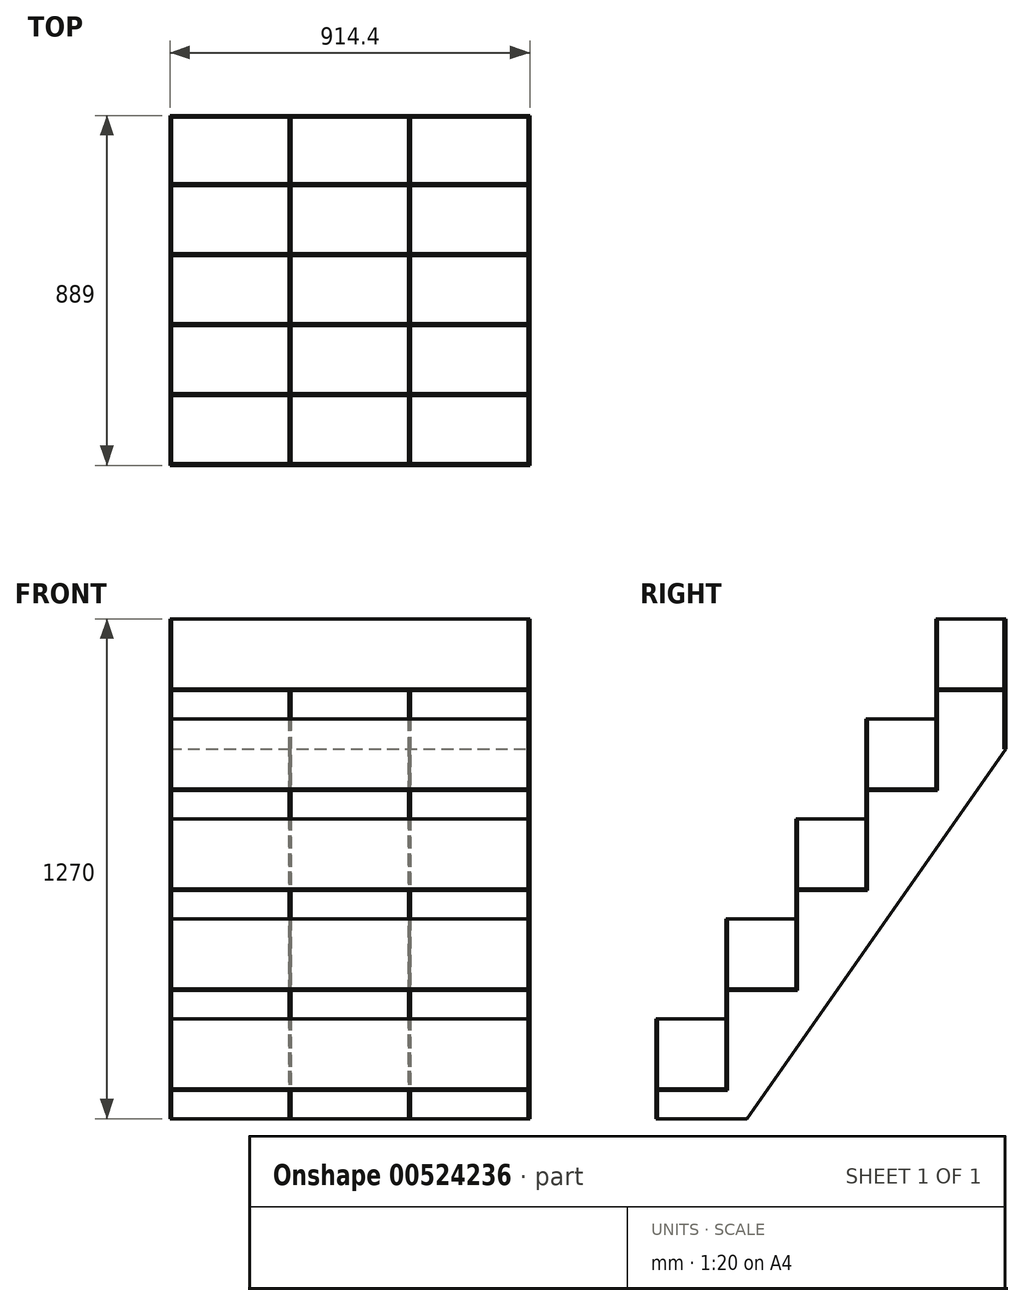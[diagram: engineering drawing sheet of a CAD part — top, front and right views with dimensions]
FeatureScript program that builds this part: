
annotation { "Feature Type Name" : "Feature", "Feature Type Description" : "" }
export const myFeature = defineFeature(function(context is Context, id is Id, definition is map)
    precondition{}
    {
        {
            assignVariable(context, id + "F0", {"name" : "matthick", "anyValue" : 4.7 * mm});
        }
        {
            var Q0;
            Q0=qCreatedBy(makeId("Right.planeOp"),FACE);
            var sketch = newSketch(context, id + "F1", { "sketchPlane" : qUnion([Q0])});
            skLineSegment(sketch, "E0", {"start": v(-436.82, -657.41) * mm, "end": v(-205.43, -657.41) * mm});
            skLineSegment(sketch, "E1", {"start": v(-205.43, -657.41) * mm, "end": v(452.18, 281.76) * mm});
            skLineSegment(sketch, "E2", {"start": v(452.18, 281.76) * mm, "end": v(452.18, 612.59) * mm});
            skLineSegment(sketch, "E3", {"start": v(452.18, 612.59) * mm, "end": v(274.38, 612.59) * mm});
            skLineSegment(sketch, "E4", {"start": v(274.38, 612.59) * mm, "end": v(274.38, 358.59) * mm});
            skLineSegment(sketch, "E5", {"start": v(274.38, 358.59) * mm, "end": v(96.58, 358.59) * mm});
            skLineSegment(sketch, "E6", {"start": v(96.58, 358.59) * mm, "end": v(96.58, 104.59) * mm});
            skLineSegment(sketch, "E7", {"start": v(96.58, 104.59) * mm, "end": v(-81.22, 104.59) * mm});
            skLineSegment(sketch, "E8", {"start": v(-81.22, 104.59) * mm, "end": v(-81.22, -149.41) * mm});
            skLineSegment(sketch, "E9", {"start": v(-81.22, -149.41) * mm, "end": v(-259.02, -149.41) * mm});
            skLineSegment(sketch, "E10", {"start": v(-259.02, -149.41) * mm, "end": v(-259.02, -403.41) * mm});
            skLineSegment(sketch, "E11", {"start": v(-259.02, -403.41) * mm, "end": v(-436.82, -403.41) * mm});
            skLineSegment(sketch, "E12", {"start": v(-436.82, -403.41) * mm, "end": v(-436.82, -657.41) * mm});
            skSolve(sketch);
        }
        {
            var Q0;
            Q0=qSketchRegion(id+"F1",true);
            extrude(context, id + "F2", {"entities" : qUnion([Q0]), "depth" : getVariable(context, 'matthick'), "offsetDistance" : 25.4 * mm});
        }
        {
            var Q0;
            Q0=makeQuery(id+"F2.opExtrude","CAP_FACE",FACE,{"disambiguationData":[OSD([sQuery(id+"F1.wireOp",EDGE,"E0"),sQuery(id+"F1.wireOp",EDGE,"E1"),sQuery(id+"F1.wireOp",EDGE,"E2"),sQuery(id+"F1.wireOp",EDGE,"E3"),sQuery(id+"F1.wireOp",EDGE,"E4"),sQuery(id+"F1.wireOp",EDGE,"E5"),sQuery(id+"F1.wireOp",EDGE,"E6"),sQuery(id+"F1.wireOp",EDGE,"E7"),sQuery(id+"F1.wireOp",EDGE,"E8"),sQuery(id+"F1.wireOp",EDGE,"E9"),sQuery(id+"F1.wireOp",EDGE,"E10"),sQuery(id+"F1.wireOp",EDGE,"E11"),sQuery(id+"F1.wireOp",EDGE,"E12")])],"isStart":false});
            var sketch = newSketch(context, id + "F3", { "sketchPlane" : qUnion([Q0])});
            skLineSegment(sketch, "E13", {"start": v(274.38, 612.59) * mm, "end": v(274.38, 434.79) * mm, "construction": true});
            skLineSegment(sketch, "E14.bottom", {"start": v(274.38, 434.79) * mm, "end": v(452.18, 434.79) * mm});
            skLineSegment(sketch, "E14.top", {"start": v(274.38, 430.09) * mm, "end": v(452.18, 430.09) * mm});
            skLineSegment(sketch, "E14.left", {"start": v(274.38, 434.79) * mm, "end": v(274.38, 430.09) * mm});
            skLineSegment(sketch, "E14.right", {"start": v(452.18, 434.79) * mm, "end": v(452.18, 430.09) * mm});
            skSolve(sketch);
        }
        {
            var Q0;
            Q0=makeQuery(id+"F3.imprint","IMPRINT",FACE,{"disambiguationData":[TD([[makeQuery(id+"F3.imprint","IMPRINT",EDGE,{"derivedFrom":sQuery(id+"F3.wireOp",EDGE,"E14.bottom")}),-1.0]])]});
            extrude(context, id + "F4", {"entities" : qUnion([Q0]), "oppositeDirection" : true, "depth" : 914.4 * mm, "offsetDistance" : 25.4 * mm});
        }
        {
            var Q0;
            Q0=makeQuery(id+"F4.opExtrude","SWEPT_BODY",BODY,{"disambiguationData":[OSD([sQuery(id+"F3.wireOp",EDGE,"E14.bottom"),sQuery(id+"F3.wireOp",EDGE,"E14.top"),sQuery(id+"F3.wireOp",EDGE,"E14.left"),sQuery(id+"F3.wireOp",EDGE,"E14.right")])]});
            var Q1;
            Q1=sQuery(id+"F1.wireOp",EDGE,"E4");
            var Q2;
            Q2=sQuery(id+"F1.wireOp",EDGE,"E5");
            transform(context, id + "F5", {"entities" : qUnion([Q0]), "transformType" : TransformType.TRANSLATION_3D, "dx" : 0 * mm, "dy" : -177.8 * mm, "dz" : -254 * mm, "makeCopy" : true});
        }
        {
            var Q0;
            Q0=makeQuery(id+"F2.opExtrude","CAP_FACE",FACE,{"disambiguationData":[OSD([sQuery(id+"F1.wireOp",EDGE,"E0"),sQuery(id+"F1.wireOp",EDGE,"E1"),sQuery(id+"F1.wireOp",EDGE,"E2"),sQuery(id+"F1.wireOp",EDGE,"E3"),sQuery(id+"F1.wireOp",EDGE,"E4"),sQuery(id+"F1.wireOp",EDGE,"E5"),sQuery(id+"F1.wireOp",EDGE,"E6"),sQuery(id+"F1.wireOp",EDGE,"E7"),sQuery(id+"F1.wireOp",EDGE,"E8"),sQuery(id+"F1.wireOp",EDGE,"E9"),sQuery(id+"F1.wireOp",EDGE,"E10"),sQuery(id+"F1.wireOp",EDGE,"E11"),sQuery(id+"F1.wireOp",EDGE,"E12")])],"isStart":false});
            var sketch = newSketch(context, id + "F6", { "sketchPlane" : qUnion([Q0])});
            skLineSegment(sketch, "E15.bottom", {"start": v(274.38, 612.59) * mm, "end": v(279.08, 612.59) * mm});
            skLineSegment(sketch, "E15.top", {"start": v(274.38, 176.09) * mm, "end": v(279.08, 176.09) * mm});
            skLineSegment(sketch, "E15.left", {"start": v(274.38, 612.59) * mm, "end": v(274.38, 176.09) * mm});
            skLineSegment(sketch, "E15.right", {"start": v(279.08, 612.59) * mm, "end": v(279.08, 176.09) * mm});
            skSolve(sketch);
        }
        {
            var Q0;
            Q0=qSketchRegion(id+"F6",true);
            extrude(context, id + "F7", {"entities" : qUnion([Q0]), "oppositeDirection" : true, "depth" : 914.4 * mm, "offsetDistance" : 25.4 * mm});
        }
        {
            var Q0;
            Q0=makeQuery(id+"F5.opPattern","COPY",BODY,{"derivedFrom":makeQuery(id+"F4.opExtrude","SWEPT_BODY",BODY,{"disambiguationData":[OSD([sQuery(id+"F3.wireOp",EDGE,"E14.bottom"),sQuery(id+"F3.wireOp",EDGE,"E14.top"),sQuery(id+"F3.wireOp",EDGE,"E14.left"),sQuery(id+"F3.wireOp",EDGE,"E14.right")])]}),"instanceName":"1"});
            var Q1;
            Q1=makeQuery(id+"F7.opExtrude","SWEPT_BODY",BODY,{"disambiguationData":[OSD([sQuery(id+"F6.wireOp",EDGE,"E15.bottom"),sQuery(id+"F6.wireOp",EDGE,"E15.top"),sQuery(id+"F6.wireOp",EDGE,"E15.left"),sQuery(id+"F6.wireOp",EDGE,"E15.right")])]});
            transform(context, id + "F8", {"entities" : qUnion([Q0, Q1]), "transformType" : TransformType.TRANSLATION_3D, "dx" : 0 * mm, "dy" : -177.8 * mm, "dz" : -254 * mm, "makeCopy" : true});
        }
        {
            var Q0;
            Q0=makeQuery(id+"F8.opPattern","COPY",BODY,{"derivedFrom":makeQuery(id+"F5.opPattern","COPY",BODY,{"derivedFrom":makeQuery(id+"F4.opExtrude","SWEPT_BODY",BODY,{"disambiguationData":[OSD([sQuery(id+"F3.wireOp",EDGE,"E14.bottom"),sQuery(id+"F3.wireOp",EDGE,"E14.top"),sQuery(id+"F3.wireOp",EDGE,"E14.left"),sQuery(id+"F3.wireOp",EDGE,"E14.right")])]}),"instanceName":"1"}),"instanceName":"1"});
            var Q1;
            Q1=makeQuery(id+"F8.opPattern","COPY",BODY,{"derivedFrom":makeQuery(id+"F7.opExtrude","SWEPT_BODY",BODY,{"disambiguationData":[OSD([sQuery(id+"F6.wireOp",EDGE,"E15.bottom"),sQuery(id+"F6.wireOp",EDGE,"E15.top"),sQuery(id+"F6.wireOp",EDGE,"E15.left"),sQuery(id+"F6.wireOp",EDGE,"E15.right")])]}),"instanceName":"1"});
            transform(context, id + "F9", {"entities" : qUnion([Q0, Q1]), "transformType" : TransformType.TRANSLATION_3D, "dx" : 0 * mm, "dy" : -177.8 * mm, "dz" : -254 * mm, "makeCopy" : true});
        }
        {
            var Q0;
            Q0=makeQuery(id+"F9.opPattern","COPY",BODY,{"derivedFrom":makeQuery(id+"F8.opPattern","COPY",BODY,{"derivedFrom":makeQuery(id+"F5.opPattern","COPY",BODY,{"derivedFrom":makeQuery(id+"F4.opExtrude","SWEPT_BODY",BODY,{"disambiguationData":[OSD([sQuery(id+"F3.wireOp",EDGE,"E14.bottom"),sQuery(id+"F3.wireOp",EDGE,"E14.top"),sQuery(id+"F3.wireOp",EDGE,"E14.left"),sQuery(id+"F3.wireOp",EDGE,"E14.right")])]}),"instanceName":"1"}),"instanceName":"1"}),"instanceName":"1"});
            var Q1;
            Q1=makeQuery(id+"F9.opPattern","COPY",BODY,{"derivedFrom":makeQuery(id+"F8.opPattern","COPY",BODY,{"derivedFrom":makeQuery(id+"F7.opExtrude","SWEPT_BODY",BODY,{"disambiguationData":[OSD([sQuery(id+"F6.wireOp",EDGE,"E15.bottom"),sQuery(id+"F6.wireOp",EDGE,"E15.top"),sQuery(id+"F6.wireOp",EDGE,"E15.left"),sQuery(id+"F6.wireOp",EDGE,"E15.right")])]}),"instanceName":"1"}),"instanceName":"1"});
            transform(context, id + "F10", {"entities" : qUnion([Q0, Q1]), "transformType" : TransformType.TRANSLATION_3D, "dx" : 0 * mm, "dy" : -177.8 * mm, "dz" : -254 * mm, "makeCopy" : true});
        }
        {
            var Q0;
            Q0=makeQuery(id+"F2.opExtrude","SWEPT_BODY",BODY,{"disambiguationData":[OSD([sQuery(id+"F1.wireOp",EDGE,"E0"),sQuery(id+"F1.wireOp",EDGE,"E1"),sQuery(id+"F1.wireOp",EDGE,"E2"),sQuery(id+"F1.wireOp",EDGE,"E3"),sQuery(id+"F1.wireOp",EDGE,"E4"),sQuery(id+"F1.wireOp",EDGE,"E5"),sQuery(id+"F1.wireOp",EDGE,"E6"),sQuery(id+"F1.wireOp",EDGE,"E7"),sQuery(id+"F1.wireOp",EDGE,"E8"),sQuery(id+"F1.wireOp",EDGE,"E9"),sQuery(id+"F1.wireOp",EDGE,"E10"),sQuery(id+"F1.wireOp",EDGE,"E11"),sQuery(id+"F1.wireOp",EDGE,"E12")])]});
            var Q1;
            Q1=makeQuery(id+"F7.opExtrude","SWEPT_EDGE",EDGE,{"disambiguationData":[OSD([sQuery(id+"F6.wireOp",EDGE,"E15.bottom"),sQuery(id+"F6.wireOp",EDGE,"E15.left")])]});
            transform(context, id + "F11", {"entities" : qUnion([Q0]), "transformType" : TransformType.TRANSLATION_3D, "dx" : -914.4 * mm + getVariable(context, 'matthick'), "dy" : 0 * mm, "dz" : 0 * mm, "makeCopy" : true});
        }
        {
            var Q0;
            Q0=makeQuery(id+"F2.opExtrude","CAP_FACE",FACE,{"disambiguationData":[OSD([sQuery(id+"F1.wireOp",EDGE,"E0"),sQuery(id+"F1.wireOp",EDGE,"E1"),sQuery(id+"F1.wireOp",EDGE,"E2"),sQuery(id+"F1.wireOp",EDGE,"E3"),sQuery(id+"F1.wireOp",EDGE,"E4"),sQuery(id+"F1.wireOp",EDGE,"E5"),sQuery(id+"F1.wireOp",EDGE,"E6"),sQuery(id+"F1.wireOp",EDGE,"E7"),sQuery(id+"F1.wireOp",EDGE,"E8"),sQuery(id+"F1.wireOp",EDGE,"E9"),sQuery(id+"F1.wireOp",EDGE,"E10"),sQuery(id+"F1.wireOp",EDGE,"E11"),sQuery(id+"F1.wireOp",EDGE,"E12")])],"isStart":false});
            var sketch = newSketch(context, id + "F12", { "sketchPlane" : qUnion([Q0])});
            skLineSegment(sketch, "E16.bottom", {"start": v(-436.82, -403.41) * mm, "end": v(-432.12, -403.41) * mm});
            skLineSegment(sketch, "E16.top", {"start": v(-436.82, -657.41) * mm, "end": v(-432.12, -657.41) * mm});
            skLineSegment(sketch, "E16.left", {"start": v(-436.82, -403.41) * mm, "end": v(-436.82, -657.41) * mm});
            skLineSegment(sketch, "E16.right", {"start": v(-432.12, -403.41) * mm, "end": v(-432.12, -657.41) * mm});
            skSolve(sketch);
        }
        {
            var Q0;
            Q0=qSketchRegion(id+"F12",true);
            extrude(context, id + "F13", {"entities" : qUnion([Q0]), "oppositeDirection" : true, "depth" : 914.4 * mm, "offsetDistance" : 25.4 * mm});
        }
        {
            var Q0;
            Q0=makeQuery(id+"F2.opExtrude","CAP_FACE",FACE,{"disambiguationData":[OSD([sQuery(id+"F1.wireOp",EDGE,"E0"),sQuery(id+"F1.wireOp",EDGE,"E1"),sQuery(id+"F1.wireOp",EDGE,"E2"),sQuery(id+"F1.wireOp",EDGE,"E3"),sQuery(id+"F1.wireOp",EDGE,"E4"),sQuery(id+"F1.wireOp",EDGE,"E5"),sQuery(id+"F1.wireOp",EDGE,"E6"),sQuery(id+"F1.wireOp",EDGE,"E7"),sQuery(id+"F1.wireOp",EDGE,"E8"),sQuery(id+"F1.wireOp",EDGE,"E9"),sQuery(id+"F1.wireOp",EDGE,"E10"),sQuery(id+"F1.wireOp",EDGE,"E11"),sQuery(id+"F1.wireOp",EDGE,"E12")])],"isStart":false});
            var sketch = newSketch(context, id + "F14", { "sketchPlane" : qUnion([Q0])});
            skLineSegment(sketch, "E17.bottom", {"start": v(452.18, 612.59) * mm, "end": v(447.48, 612.59) * mm});
            skLineSegment(sketch, "E17.top", {"start": v(452.18, 281.76) * mm, "end": v(447.48, 281.76) * mm});
            skLineSegment(sketch, "E17.left", {"start": v(452.18, 612.59) * mm, "end": v(452.18, 281.76) * mm});
            skLineSegment(sketch, "E17.right", {"start": v(447.48, 612.59) * mm, "end": v(447.48, 281.76) * mm});
            skSolve(sketch);
        }
        {
            var Q0;
            Q0=qSketchRegion(id+"F14",true);
            extrude(context, id + "F15", {"entities" : qUnion([Q0]), "oppositeDirection" : true, "depth" : 914.4 * mm, "offsetDistance" : 25.4 * mm});
        }
        {
            var Q0;
            Q0=makeQuery(id+"F2.opExtrude","CAP_FACE",FACE,{"disambiguationData":[OSD([sQuery(id+"F1.wireOp",EDGE,"E0"),sQuery(id+"F1.wireOp",EDGE,"E1"),sQuery(id+"F1.wireOp",EDGE,"E2"),sQuery(id+"F1.wireOp",EDGE,"E3"),sQuery(id+"F1.wireOp",EDGE,"E4"),sQuery(id+"F1.wireOp",EDGE,"E5"),sQuery(id+"F1.wireOp",EDGE,"E6"),sQuery(id+"F1.wireOp",EDGE,"E7"),sQuery(id+"F1.wireOp",EDGE,"E8"),sQuery(id+"F1.wireOp",EDGE,"E9"),sQuery(id+"F1.wireOp",EDGE,"E10"),sQuery(id+"F1.wireOp",EDGE,"E11"),sQuery(id+"F1.wireOp",EDGE,"E12")])],"isStart":false});
            var sketch = newSketch(context, id + "F16", { "sketchPlane" : qUnion([Q0])});
            skLineSegment(sketch, "E18", {"start": v(-436.82, -657.41) * mm, "end": v(-205.43, -657.41) * mm});
            skLineSegment(sketch, "E19", {"start": v(-205.43, -657.41) * mm, "end": v(452.18, 281.76) * mm});
            skLineSegment(sketch, "E20", {"start": v(452.18, 281.76) * mm, "end": v(452.18, 434.79) * mm});
            skLineSegment(sketch, "E21", {"start": v(452.18, 434.79) * mm, "end": v(274.38, 434.79) * mm});
            skLineSegment(sketch, "E22", {"start": v(274.38, 434.79) * mm, "end": v(274.38, 180.79) * mm});
            skLineSegment(sketch, "E23", {"start": v(274.38, 180.79) * mm, "end": v(96.58, 180.79) * mm});
            skLineSegment(sketch, "E24", {"start": v(96.58, 180.79) * mm, "end": v(96.58, -73.21) * mm});
            skLineSegment(sketch, "E25", {"start": v(96.58, -73.21) * mm, "end": v(-81.22, -73.21) * mm});
            skLineSegment(sketch, "E26", {"start": v(-81.22, -73.21) * mm, "end": v(-81.22, -327.21) * mm});
            skLineSegment(sketch, "E27", {"start": v(-81.22, -327.21) * mm, "end": v(-259.02, -327.21) * mm});
            skLineSegment(sketch, "E28", {"start": v(-259.02, -327.21) * mm, "end": v(-259.02, -581.21) * mm});
            skLineSegment(sketch, "E29", {"start": v(-259.02, -581.21) * mm, "end": v(-436.82, -581.21) * mm});
            skLineSegment(sketch, "E30", {"start": v(-436.82, -581.21) * mm, "end": v(-436.82, -657.41) * mm});
            skSolve(sketch);
        }
        {
            var Q0;
            Q0=makeQuery(id+"F16.imprint","IMPRINT",FACE,{"disambiguationData":[TD([[makeQuery(id+"F16.imprint","IMPRINT",EDGE,{"derivedFrom":sQuery(id+"F16.wireOp",EDGE,"E19")}),1.0]])]});
            extrude(context, id + "F17", {"entities" : qUnion([Q0]), "oppositeDirection" : true, "depth" : getVariable(context, 'matthick'), "offsetDistance" : 25.4 * mm});
        }
        {
            var Q0;
            Q0=makeQuery(id+"F17.opExtrude","SWEPT_BODY",BODY,{"disambiguationData":[OSD([sQuery(id+"F1.wireOp",EDGE,"E0"),sQuery(id+"F16.wireOp",EDGE,"E19"),sQuery(id+"F16.wireOp",EDGE,"E20"),sQuery(id+"F16.wireOp",EDGE,"E21"),sQuery(id+"F16.wireOp",EDGE,"E22"),sQuery(id+"F16.wireOp",EDGE,"E23"),sQuery(id+"F16.wireOp",EDGE,"E24"),sQuery(id+"F16.wireOp",EDGE,"E25"),sQuery(id+"F16.wireOp",EDGE,"E26"),sQuery(id+"F16.wireOp",EDGE,"E27"),sQuery(id+"F16.wireOp",EDGE,"E28"),sQuery(id+"F16.wireOp",EDGE,"E29"),sQuery(id+"F16.wireOp",EDGE,"E30")])]});
            transform(context, id + "F18", {"entities" : qUnion([Q0]), "transformType" : TransformType.TRANSLATION_3D, "dx" : -304.8 * mm + getVariable(context, 'matthick') * .3333, "dy" : 0 * mm, "dz" : 0 * mm, "makeCopy" : false});
        }
        {
            var Q0;
            Q0=makeQuery(id+"F17.opExtrude","SWEPT_BODY",BODY,{"disambiguationData":[OSD([sQuery(id+"F1.wireOp",EDGE,"E0"),sQuery(id+"F16.wireOp",EDGE,"E19"),sQuery(id+"F16.wireOp",EDGE,"E20"),sQuery(id+"F16.wireOp",EDGE,"E21"),sQuery(id+"F16.wireOp",EDGE,"E22"),sQuery(id+"F16.wireOp",EDGE,"E23"),sQuery(id+"F16.wireOp",EDGE,"E24"),sQuery(id+"F16.wireOp",EDGE,"E25"),sQuery(id+"F16.wireOp",EDGE,"E26"),sQuery(id+"F16.wireOp",EDGE,"E27"),sQuery(id+"F16.wireOp",EDGE,"E28"),sQuery(id+"F16.wireOp",EDGE,"E29"),sQuery(id+"F16.wireOp",EDGE,"E30")])]});
            transform(context, id + "F19", {"entities" : qUnion([Q0]), "transformType" : TransformType.TRANSLATION_3D, "dx" : -304.8 * mm + getVariable(context, 'matthick') * .3333, "dy" : 0 * mm, "dz" : 0 * mm, "makeCopy" : true});
        }
    });
